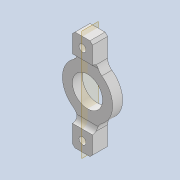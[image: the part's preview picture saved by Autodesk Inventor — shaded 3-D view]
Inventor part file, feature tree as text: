
AUTODESK INVENTOR PART (.ipt)
format: ipt  version: 2020 (Build 240168000, 168)  size: 162,816 bytes
history: native  units: mm
features: other x3, extrude x2, fillet x2, sketch x2, plane x1, chamfer x1, reference x1, projected_geometry x1
ambient origin geometry x8: Origin, YZ Plane, XZ Plane, XY Plane, X Axis, Y Axis, Z Axis, Center Point
bodies: Solid1 (feature_tree)
feature tree (13):
  extrude  "Extrusion1"  Depth=10.0mm
  extrude  "Extrusion2"  Depth=1.0mm
  plane  "Work Plane1"
  chamfer  "Chamfer1"  Distance=8.0mm
  fillet  "Fillet1"  Radius=1.4mm
  fillet  "Fillet2"  Radius=4.0mm
  sketch  "Sketch1"  dims[d0=6.0mm d1=10.0mm]
  reference  "Reference1"
  sketch  "Sketch2"  dims[d2=8.0mm d3=1.4mm d4=8.0mm d5=1.4mm d6=4.0mm d7=20.0mm d8=2.0mm d9=0.0mm d10=4.0mm d11=4.0mm d12=1.0mm d13=0.0mm d14=0.5mm d15=2.0mm d16=45.0deg d17=2.0mm d18=1.0mm]
  projected_geometry  "Projected Loop1"
  parser-record x1  (decoder bookkeeping rows leaked as tree rows — omitted from the tree; the rows remain in map.json)
  other  "tip_3_ass.iam"
  other  "bearing_3_6_2:2"
note: 1 file-system path scrubbed to <path> (originals preserved in map.json)
